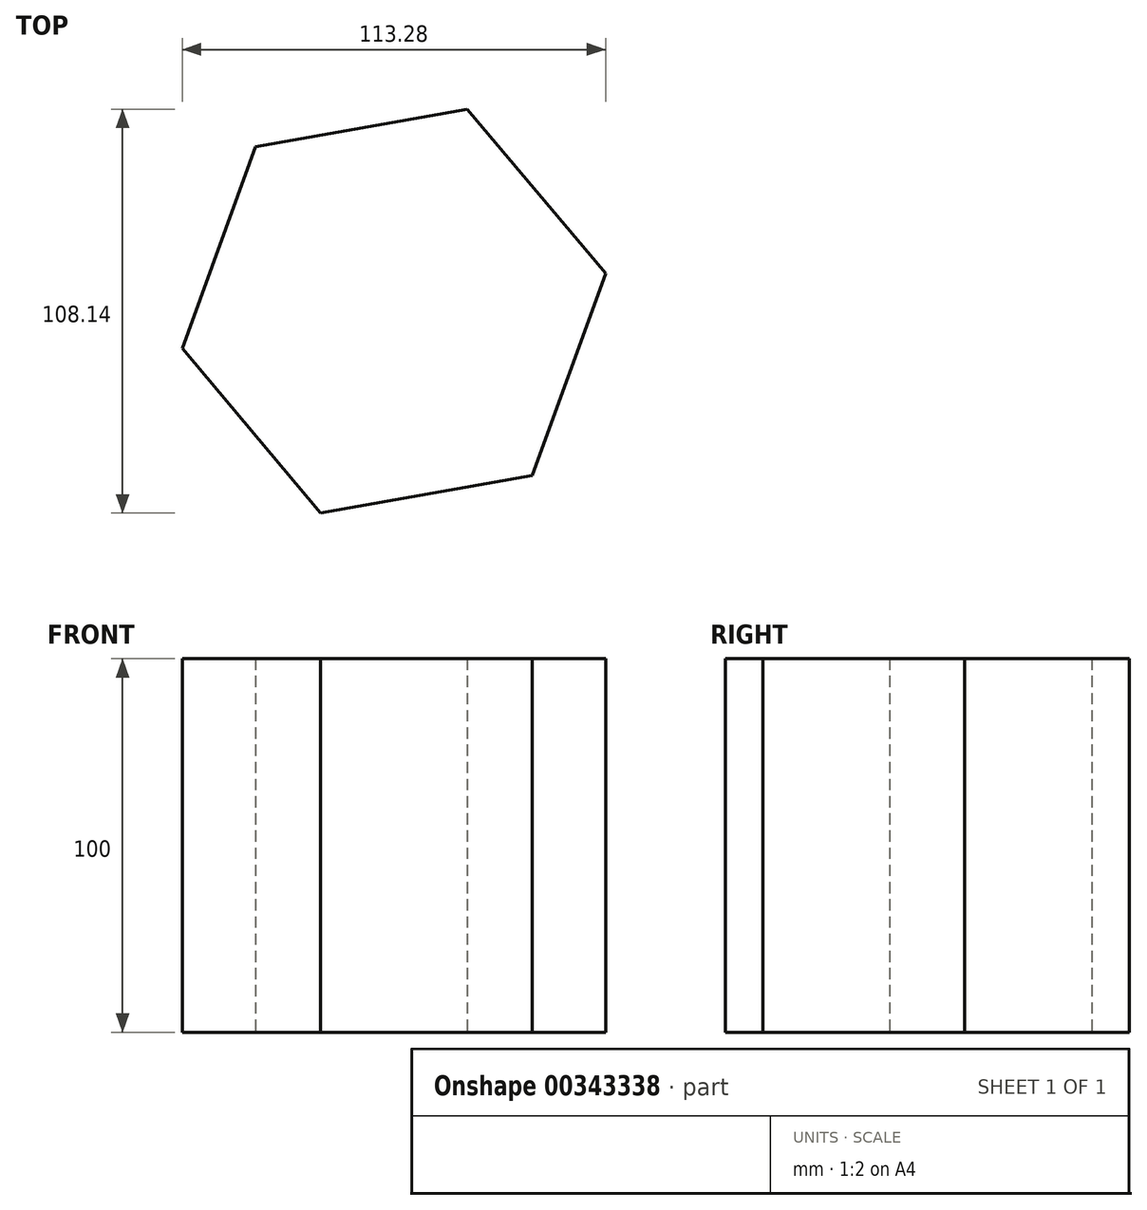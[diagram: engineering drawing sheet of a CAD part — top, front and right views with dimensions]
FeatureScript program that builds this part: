
annotation { "Feature Type Name" : "Feature", "Feature Type Description" : "" }
export const myFeature = defineFeature(function(context is Context, id is Id, definition is map)
    precondition{}
    {
        {
            var Q0;
            Q0=qCreatedBy(makeId("Top.planeOp"),FACE);
            var sketch = newSketch(context, id + "F0", { "sketchPlane" : qUnion([Q0])});
            skCircle(sketch, "E0.cCircle", {"center": v(0, 0) * mm, "radius": 57.52 * mm, "construction": true});
            skLineSegment(sketch, "E0.0", {"start": v(-37, 44.04) * mm, "end": v(19.63, 54.07) * mm});
            skLineSegment(sketch, "E0.1", {"start": v(19.63, 54.07) * mm, "end": v(56.64, 10.03) * mm});
            skLineSegment(sketch, "E0.2", {"start": v(56.64, 10.03) * mm, "end": v(37, -44.04) * mm});
            skLineSegment(sketch, "E0.3", {"start": v(37, -44.04) * mm, "end": v(-19.63, -54.07) * mm});
            skLineSegment(sketch, "E0.4", {"start": v(-19.63, -54.07) * mm, "end": v(-56.64, -10.03) * mm});
            skLineSegment(sketch, "E0.5", {"start": v(-56.64, -10.03) * mm, "end": v(-37, 44.04) * mm});
            skSolve(sketch);
        }
        {
            var Q0;
            Q0=makeQuery(id+"F0.imprint","IMPRINT",FACE,{"disambiguationData":[TD([[makeQuery(id+"F0.imprint","IMPRINT",EDGE,{"derivedFrom":sQuery(id+"F0.wireOp",EDGE,"E0.0")}),-1.0]])]});
            extrude(context, id + "F1", {"entities" : qUnion([Q0]), "depth" : 100 * mm});
        }
    });
